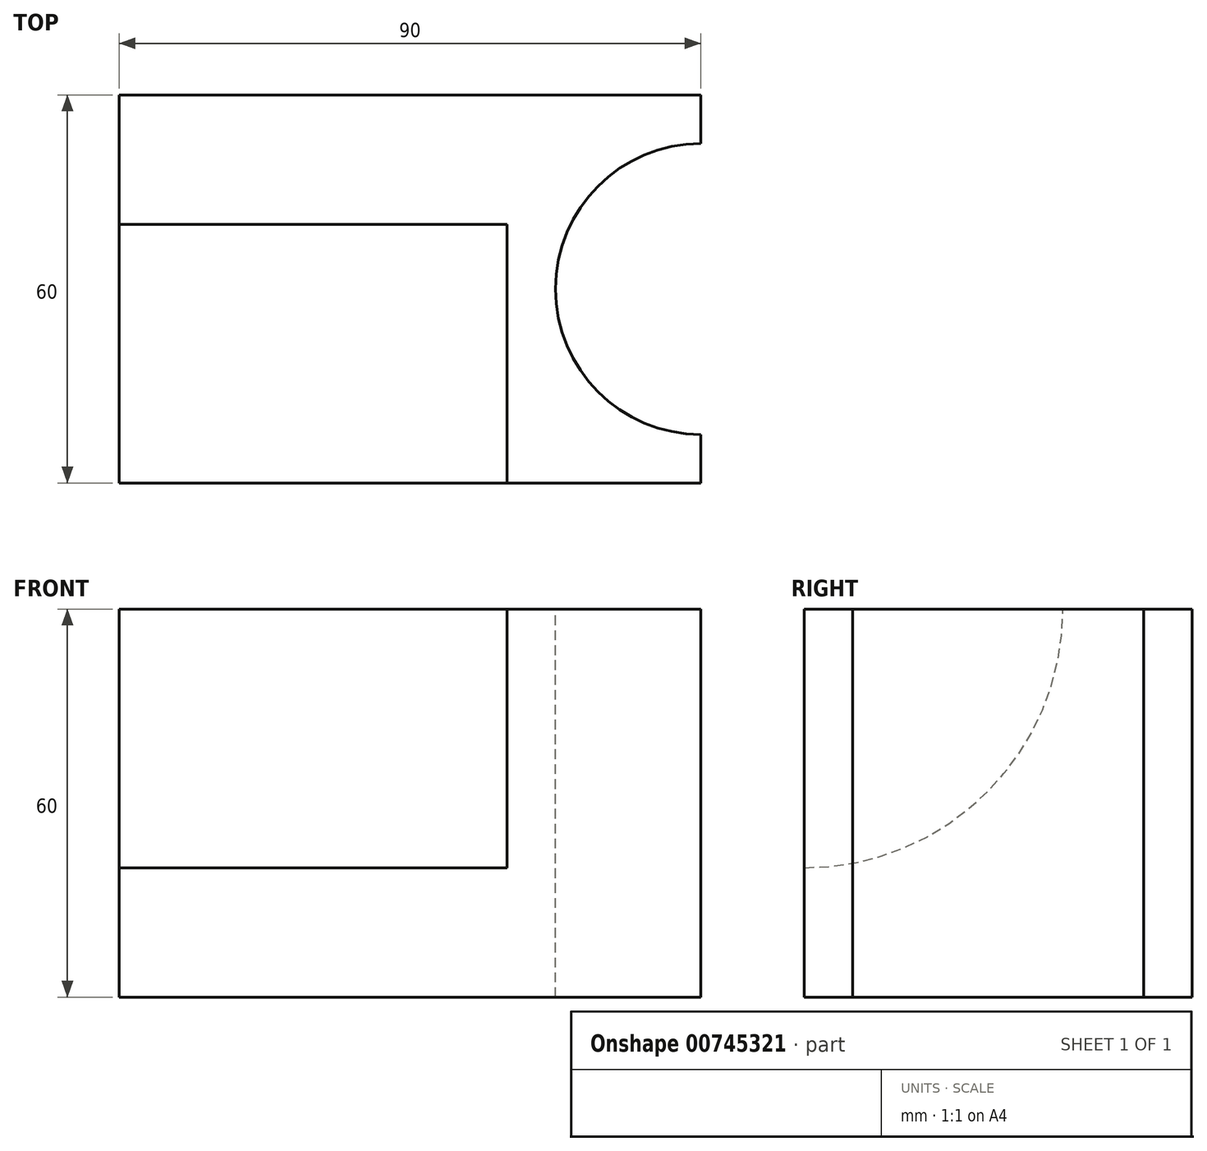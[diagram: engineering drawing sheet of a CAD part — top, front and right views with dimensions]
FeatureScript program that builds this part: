
annotation { "Feature Type Name" : "Feature", "Feature Type Description" : "" }
export const myFeature = defineFeature(function(context is Context, id is Id, definition is map)
    precondition{}
    {
        {
            var Q0;
            Q0=qCreatedBy(makeId("Top.planeOp"),FACE);
            var sketch = newSketch(context, id + "F0", { "sketchPlane" : qUnion([Q0])});
            skLineSegment(sketch, "E0.bottom", {"start": v(0, 60) * mm, "end": v(90, 60) * mm});
            skLineSegment(sketch, "E0.top", {"start": v(0, 0) * mm, "end": v(90, 0) * mm});
            skLineSegment(sketch, "E0.left", {"start": v(0, 60) * mm, "end": v(0, 0) * mm});
            skLineSegment(sketch, "E0.right", {"start": v(90, 60) * mm, "end": v(90, 0) * mm});
            skSolve(sketch);
        }
        {
            var Q0;
            Q0 = qSketchRegion(id + "F0", true);
            extrude(context, id + "F1", {"entities" : qUnion([Q0]), "depth" : 60 * mm, "offsetDistance" : 25 * mm});
        }
        {
            var Q0;
            Q0=makeQuery(id+"F1.opExtrude","CAP_FACE",FACE,{"disambiguationData":[OSD([sQuery(id+"F0.wireOp",EDGE,"E0.bottom"),sQuery(id+"F0.wireOp",EDGE,"E0.top"),sQuery(id+"F0.wireOp",EDGE,"E0.left"),sQuery(id+"F0.wireOp",EDGE,"E0.right")])],"isStart":false});
            var sketch = newSketch(context, id + "F2", { "sketchPlane" : qUnion([Q0])});
            skArc(sketch, "E1", {"start": v(90, 52.5) * mm, "mid": v(67.5, 30) * mm, "end": v(90, 7.5) * mm});
            skSolve(sketch);
        }
        {
            var Q0;
            Q0 = qSketchRegion(id + "F2", true);
            var Q1;
            {var subQ0=sQuery(id+"F2.wireOp",EDGE,"E1");Q1=makeQuery(id+"F2.imprint","IMPRINT",FACE,{"disambiguationData":[TD([[makeQuery(id+"F2.imprint","IMPRINT",EDGE,{"derivedFrom":subQ0}),1.0]])]});}
            extrude(context, id + "F3", {"entities" : qUnion([Q0, Q1]), "operationType" : NewBodyOperationType.REMOVE, "oppositeDirection" : true, "depth" : 60 * mm, "offsetDistance" : 25 * mm});
        }
        {
            var Q0;
            Q0=makeQuery(id+"F1.opExtrude","SWEPT_FACE",FACE,{"disambiguationData":[OSD([sQuery(id+"F0.wireOp",EDGE,"E0.left")])]});
            var sketch = newSketch(context, id + "F4", { "sketchPlane" : qUnion([Q0])});
            skArc(sketch, "E2", {"start": v(-40, 60) * mm, "mid": v(-28.28, 31.72) * mm, "end": v(0, 20) * mm});
            skSolve(sketch);
        }
        {
            var Q0;
            Q0 = qSketchRegion(id + "F4", true);
            var Q1;
            {var subQ0=sQuery(id+"F4.wireOp",EDGE,"E2");Q1=makeQuery(id+"F4.imprint","IMPRINT",FACE,{"disambiguationData":[TD([[makeQuery(id+"F4.imprint","IMPRINT",EDGE,{"derivedFrom":subQ0}),1.0]])]});}
            extrude(context, id + "F5", {"entities" : qUnion([Q0, Q1]), "operationType" : NewBodyOperationType.REMOVE, "oppositeDirection" : true, "depth" : 60 * mm, "offsetDistance" : 25 * mm});
        }
    });
